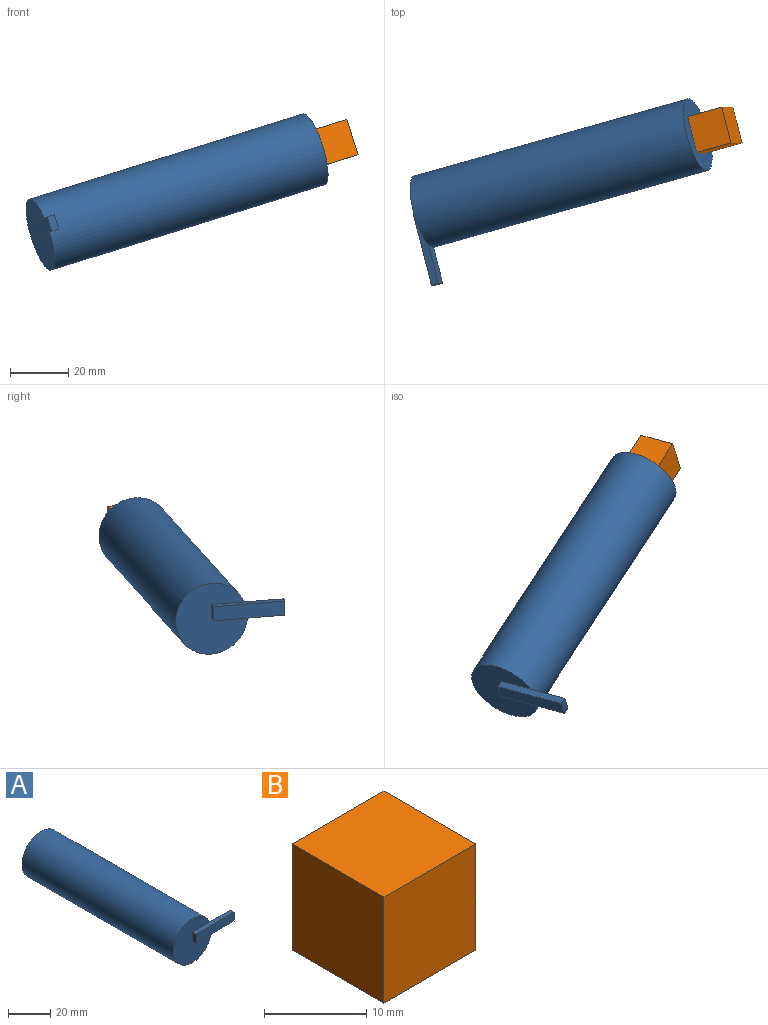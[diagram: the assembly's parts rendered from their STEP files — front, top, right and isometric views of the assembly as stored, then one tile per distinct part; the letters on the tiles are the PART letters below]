
ASSEMBLY  parts=2 mates=1
PART A: 9 faces, bbox 38.1x104.1x25.4 mm
  f0: plane 25.4x25.4mm, normal (0,-1,0), area 444mm2, adj f1,f4,f5,f6
  f1: cylinder r=12.7mm len=101.6mm, axis (0,1,0), area 8107.3mm2, adj f0,f2,f3
  f2: plane 25.4x25.4mm, normal (0,1,0), area 506.7mm2, adj f1
  f3: plane 13.76x5.08mm, normal (0,1,0), area 66.3mm2, adj f1,f4,f6,f7
  f4: plane 25.4x2.54mm, normal (0,0,1), area 64.5mm2, adj f0,f3,f5,f7,f8
  f5: plane 5.08x2.54mm, normal (-1,0,0), area 12.9mm2, adj f0,f4,f6,f8
  f6: plane 25.4x2.54mm, normal (0,0,-1), area 64.5mm2, adj f0,f3,f5,f7,f8
  f7: plane 5.08x2.54mm, normal (1,0,0), area 12.9mm2, adj f3,f4,f6,f8
  f8: plane 25.4x5.08mm, normal (0,-1,0), area 129mm2, adj f4,f5,f6,f7
PART B: 6 faces, bbox 12.7x12.7x12.7 mm
  f0: plane 12.7x12.7mm, normal (0,0,-1), area 161.3mm2, adj f1,f3,f4,f5
  f1: plane 12.7x12.7mm, normal (1,0,0), area 161.3mm2, adj f0,f2,f4,f5
  f2: plane 12.7x12.7mm, normal (0,0,1), area 161.3mm2, adj f1,f3,f4,f5
  f3: plane 12.7x12.7mm, normal (-1,0,0), area 161.3mm2, adj f0,f2,f4,f5
  f4: plane 12.7x12.7mm, normal (0,-1,0), area 161.3mm2, adj f0,f1,f2,f3
  f5: plane 12.7x12.7mm, normal (0,1,0), area 161.3mm2, adj f0,f1,f2,f3
PLACE A rot(axis=(0.15,-0.19,-0.97),76.7deg) t=(6.22,-37.35,-14.68)mm
PLACE B rot(axis=(0.15,-0.19,-0.97),76.7deg) t=(26.45,-34.06,-38.29)mm
MATE slider B.f4 <-> A.f1  axis (-0.92,-0.26,-0.29) through (6.22,-37.35,-14.68)mm
